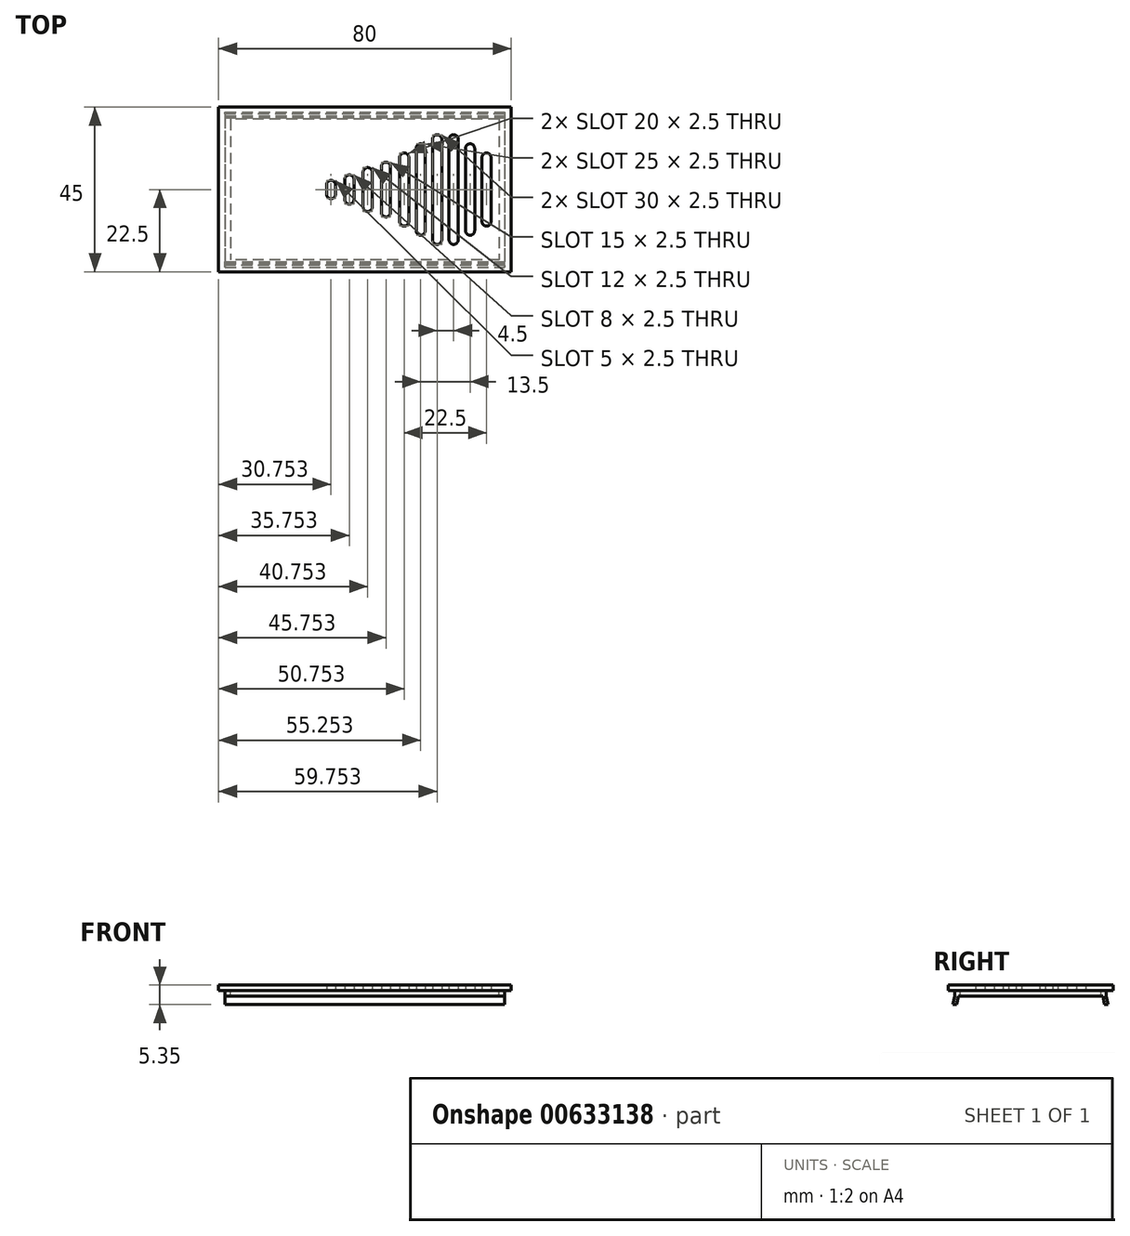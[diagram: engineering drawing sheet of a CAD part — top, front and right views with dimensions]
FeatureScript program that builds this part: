
annotation { "Feature Type Name" : "Feature", "Feature Type Description" : "" }
export const myFeature = defineFeature(function(context is Context, id is Id, definition is map)
    precondition{}
    {
        {
            var Q0;
            Q0=qCreatedBy(makeId("Top.planeOp"),FACE);
            var sketch = newSketch(context, id + "F0", { "sketchPlane" : qUnion([Q0])});
            skLineSegment(sketch, "E0.bottom", {"start": v(-39.19, 25) * mm, "end": v(40.81, 25) * mm});
            skLineSegment(sketch, "E0.top", {"start": v(-39.19, -20) * mm, "end": v(40.81, -20) * mm});
            skLineSegment(sketch, "E0.left", {"start": v(-39.19, 25) * mm, "end": v(-39.19, -20) * mm});
            skLineSegment(sketch, "E0.right", {"start": v(40.81, 25) * mm, "end": v(40.81, -20) * mm});
            skLineSegment(sketch, "E1.bottom", {"start": v(29.56, 15) * mm, "end": v(29.56, 15) * mm});
            skLineSegment(sketch, "E1.top", {"start": v(29.56, -10) * mm, "end": v(29.56, -10) * mm});
            skLineSegment(sketch, "E1.left", {"start": v(28.31, 13.75) * mm, "end": v(28.31, -8.75) * mm});
            skLineSegment(sketch, "E1.right", {"start": v(30.81, 13.75) * mm, "end": v(30.81, -8.75) * mm});
            skLineSegment(sketch, "E2.bottom", {"start": v(25.06, 17.5) * mm, "end": v(25.06, 17.5) * mm});
            skLineSegment(sketch, "E2.top", {"start": v(25.06, -12.5) * mm, "end": v(25.06, -12.5) * mm});
            skLineSegment(sketch, "E2.left", {"start": v(23.81, 16.25) * mm, "end": v(23.81, -11.25) * mm});
            skLineSegment(sketch, "E2.right", {"start": v(26.31, 16.25) * mm, "end": v(26.31, -11.25) * mm});
            skLineSegment(sketch, "E3.bottom", {"start": v(20.56, 17.5) * mm, "end": v(20.56, 17.5) * mm});
            skLineSegment(sketch, "E3.top", {"start": v(20.56, -12.5) * mm, "end": v(20.56, -12.5) * mm});
            skLineSegment(sketch, "E3.left", {"start": v(19.31, 16.25) * mm, "end": v(19.31, -11.25) * mm});
            skLineSegment(sketch, "E3.right", {"start": v(21.81, 16.25) * mm, "end": v(21.81, -11.25) * mm});
            skLineSegment(sketch, "E4.bottom", {"start": v(16.06, 15) * mm, "end": v(16.06, 15) * mm});
            skLineSegment(sketch, "E4.top", {"start": v(16.06, -10) * mm, "end": v(16.06, -10) * mm});
            skLineSegment(sketch, "E4.left", {"start": v(14.81, 13.75) * mm, "end": v(14.81, -8.75) * mm});
            skLineSegment(sketch, "E4.right", {"start": v(17.31, 13.75) * mm, "end": v(17.31, -8.75) * mm});
            skLineSegment(sketch, "E5.bottom", {"start": v(11.56, 12.5) * mm, "end": v(11.56, 12.5) * mm});
            skLineSegment(sketch, "E5.top", {"start": v(11.56, -7.5) * mm, "end": v(11.56, -7.5) * mm});
            skLineSegment(sketch, "E5.left", {"start": v(10.31, 11.25) * mm, "end": v(10.31, -6.25) * mm});
            skLineSegment(sketch, "E5.right", {"start": v(12.81, 11.25) * mm, "end": v(12.81, -6.25) * mm});
            skLineSegment(sketch, "E6.bottom", {"start": v(34.06, 12.5) * mm, "end": v(34.06, 12.5) * mm});
            skLineSegment(sketch, "E6.top", {"start": v(34.06, -7.5) * mm, "end": v(34.06, -7.5) * mm});
            skLineSegment(sketch, "E6.left", {"start": v(32.81, 11.25) * mm, "end": v(32.81, -6.25) * mm});
            skLineSegment(sketch, "E6.right", {"start": v(35.31, 11.25) * mm, "end": v(35.31, -6.25) * mm});
            skPoint(sketch, "E7.visualSharp", {"position": v(35.31, -7.5) * mm});
            skArc(sketch, "E7.filletArc", {"start": v(34.06, -7.5) * mm, "mid": v(34.95, -7.13) * mm, "end": v(35.31, -6.25) * mm});
            skPoint(sketch, "E8.visualSharp", {"position": v(32.81, -7.5) * mm});
            skArc(sketch, "E8.filletArc", {"start": v(32.81, -6.25) * mm, "mid": v(33.18, -7.13) * mm, "end": v(34.06, -7.5) * mm});
            skPoint(sketch, "E9.visualSharp", {"position": v(32.81, 12.5) * mm});
            skArc(sketch, "E9.filletArc", {"start": v(34.06, 12.5) * mm, "mid": v(33.18, 12.13) * mm, "end": v(32.81, 11.25) * mm});
            skPoint(sketch, "E10.visualSharp", {"position": v(35.31, 12.5) * mm});
            skArc(sketch, "E10.filletArc", {"start": v(35.31, 11.25) * mm, "mid": v(34.95, 12.13) * mm, "end": v(34.06, 12.5) * mm});
            skPoint(sketch, "E11.visualSharp", {"position": v(30.81, 15) * mm});
            skArc(sketch, "E11.filletArc", {"start": v(30.81, 13.75) * mm, "mid": v(30.45, 14.63) * mm, "end": v(29.56, 15) * mm});
            skPoint(sketch, "E12.visualSharp", {"position": v(28.31, 15) * mm});
            skArc(sketch, "E12.filletArc", {"start": v(29.56, 15) * mm, "mid": v(28.68, 14.63) * mm, "end": v(28.31, 13.75) * mm});
            skPoint(sketch, "E13.visualSharp", {"position": v(28.31, -10) * mm});
            skArc(sketch, "E13.filletArc", {"start": v(28.31, -8.75) * mm, "mid": v(28.68, -9.63) * mm, "end": v(29.56, -10) * mm});
            skPoint(sketch, "E14.visualSharp", {"position": v(30.81, -10) * mm});
            skArc(sketch, "E14.filletArc", {"start": v(29.56, -10) * mm, "mid": v(30.45, -9.63) * mm, "end": v(30.81, -8.75) * mm});
            skPoint(sketch, "E15.visualSharp", {"position": v(26.31, -12.5) * mm});
            skArc(sketch, "E15.filletArc", {"start": v(25.06, -12.5) * mm, "mid": v(25.95, -12.13) * mm, "end": v(26.31, -11.25) * mm});
            skPoint(sketch, "E16.visualSharp", {"position": v(23.81, -12.5) * mm});
            skArc(sketch, "E16.filletArc", {"start": v(23.81, -11.25) * mm, "mid": v(24.18, -12.13) * mm, "end": v(25.06, -12.5) * mm});
            skPoint(sketch, "E17.visualSharp", {"position": v(21.81, -12.5) * mm});
            skArc(sketch, "E17.filletArc", {"start": v(20.56, -12.5) * mm, "mid": v(21.45, -12.13) * mm, "end": v(21.81, -11.25) * mm});
            skPoint(sketch, "E18.visualSharp", {"position": v(19.31, -12.5) * mm});
            skArc(sketch, "E18.filletArc", {"start": v(19.31, -11.25) * mm, "mid": v(19.68, -12.13) * mm, "end": v(20.56, -12.5) * mm});
            skPoint(sketch, "E19.visualSharp", {"position": v(17.31, -10) * mm});
            skArc(sketch, "E19.filletArc", {"start": v(16.06, -10) * mm, "mid": v(16.95, -9.63) * mm, "end": v(17.31, -8.75) * mm});
            skPoint(sketch, "E20.visualSharp", {"position": v(14.81, -10) * mm});
            skArc(sketch, "E20.filletArc", {"start": v(14.81, -8.75) * mm, "mid": v(15.18, -9.63) * mm, "end": v(16.06, -10) * mm});
            skPoint(sketch, "E21.visualSharp", {"position": v(12.81, -7.5) * mm});
            skArc(sketch, "E21.filletArc", {"start": v(11.56, -7.5) * mm, "mid": v(12.45, -7.13) * mm, "end": v(12.81, -6.25) * mm});
            skPoint(sketch, "E22.visualSharp", {"position": v(10.31, -7.5) * mm});
            skArc(sketch, "E22.filletArc", {"start": v(10.31, -6.25) * mm, "mid": v(10.68, -7.13) * mm, "end": v(11.56, -7.5) * mm});
            skPoint(sketch, "E23.visualSharp", {"position": v(10.31, 12.5) * mm});
            skArc(sketch, "E23.filletArc", {"start": v(11.56, 12.5) * mm, "mid": v(10.68, 12.13) * mm, "end": v(10.31, 11.25) * mm});
            skPoint(sketch, "E24.visualSharp", {"position": v(12.81, 12.5) * mm});
            skArc(sketch, "E24.filletArc", {"start": v(12.81, 11.25) * mm, "mid": v(12.45, 12.13) * mm, "end": v(11.56, 12.5) * mm});
            skPoint(sketch, "E25.visualSharp", {"position": v(14.81, 15) * mm});
            skArc(sketch, "E25.filletArc", {"start": v(16.06, 15) * mm, "mid": v(15.18, 14.63) * mm, "end": v(14.81, 13.75) * mm});
            skPoint(sketch, "E26.visualSharp", {"position": v(17.31, 15) * mm});
            skArc(sketch, "E26.filletArc", {"start": v(17.31, 13.75) * mm, "mid": v(16.95, 14.63) * mm, "end": v(16.06, 15) * mm});
            skPoint(sketch, "E27.visualSharp", {"position": v(19.31, 17.5) * mm});
            skArc(sketch, "E27.filletArc", {"start": v(20.56, 17.5) * mm, "mid": v(19.68, 17.13) * mm, "end": v(19.31, 16.25) * mm});
            skPoint(sketch, "E28.visualSharp", {"position": v(21.81, 17.5) * mm});
            skArc(sketch, "E28.filletArc", {"start": v(21.81, 16.25) * mm, "mid": v(21.45, 17.13) * mm, "end": v(20.56, 17.5) * mm});
            skPoint(sketch, "E29.visualSharp", {"position": v(23.81, 17.5) * mm});
            skArc(sketch, "E29.filletArc", {"start": v(25.06, 17.5) * mm, "mid": v(24.18, 17.13) * mm, "end": v(23.81, 16.25) * mm});
            skPoint(sketch, "E30.visualSharp", {"position": v(26.31, 17.5) * mm});
            skArc(sketch, "E30.filletArc", {"start": v(26.31, 16.25) * mm, "mid": v(25.95, 17.13) * mm, "end": v(25.06, 17.5) * mm});
            skLineSegment(sketch, "E31", {"start": v(-39.19, 2.5) * mm, "end": v(40.81, 2.5) * mm, "construction": true});
            skLineSegment(sketch, "E32.bottom", {"start": v(6.56, -5) * mm, "end": v(6.56, -5) * mm});
            skLineSegment(sketch, "E32.top", {"start": v(6.56, 10) * mm, "end": v(6.56, 10) * mm});
            skLineSegment(sketch, "E32.left", {"start": v(5.31, -3.75) * mm, "end": v(5.31, 8.75) * mm});
            skLineSegment(sketch, "E32.right", {"start": v(7.81, -3.75) * mm, "end": v(7.81, 8.75) * mm});
            skLineSegment(sketch, "E33.bottom", {"start": v(1.56, -3.5) * mm, "end": v(1.56, -3.5) * mm});
            skLineSegment(sketch, "E33.top", {"start": v(1.56, 8.5) * mm, "end": v(1.56, 8.5) * mm});
            skLineSegment(sketch, "E33.left", {"start": v(0.31, -2.25) * mm, "end": v(0.31, 7.25) * mm});
            skLineSegment(sketch, "E33.right", {"start": v(2.81, -2.25) * mm, "end": v(2.81, 7.25) * mm});
            skPoint(sketch, "E34.visualSharp", {"position": v(5.31, -5) * mm});
            skArc(sketch, "E34.filletArc", {"start": v(5.31, -3.75) * mm, "mid": v(5.68, -4.63) * mm, "end": v(6.56, -5) * mm});
            skPoint(sketch, "E35.visualSharp", {"position": v(7.81, -5) * mm});
            skArc(sketch, "E35.filletArc", {"start": v(6.56, -5) * mm, "mid": v(7.45, -4.63) * mm, "end": v(7.81, -3.75) * mm});
            skPoint(sketch, "E36.visualSharp", {"position": v(5.31, 10) * mm});
            skArc(sketch, "E36.filletArc", {"start": v(6.56, 10) * mm, "mid": v(5.68, 9.63) * mm, "end": v(5.31, 8.75) * mm});
            skPoint(sketch, "E37.visualSharp", {"position": v(7.81, 10) * mm});
            skArc(sketch, "E37.filletArc", {"start": v(7.81, 8.75) * mm, "mid": v(7.45, 9.63) * mm, "end": v(6.56, 10) * mm});
            skPoint(sketch, "E38.visualSharp", {"position": v(2.81, -3.5) * mm});
            skArc(sketch, "E38.filletArc", {"start": v(1.56, -3.5) * mm, "mid": v(2.45, -3.13) * mm, "end": v(2.81, -2.25) * mm});
            skPoint(sketch, "E39.visualSharp", {"position": v(0.31, -3.5) * mm});
            skArc(sketch, "E39.filletArc", {"start": v(0.31, -2.25) * mm, "mid": v(0.68, -3.13) * mm, "end": v(1.56, -3.5) * mm});
            skPoint(sketch, "E40.visualSharp", {"position": v(0.31, 8.5) * mm});
            skArc(sketch, "E40.filletArc", {"start": v(1.56, 8.5) * mm, "mid": v(0.68, 8.13) * mm, "end": v(0.31, 7.25) * mm});
            skPoint(sketch, "E41.visualSharp", {"position": v(2.81, 8.5) * mm});
            skArc(sketch, "E41.filletArc", {"start": v(2.81, 7.25) * mm, "mid": v(2.45, 8.13) * mm, "end": v(1.56, 8.5) * mm});
            skLineSegment(sketch, "E42.bottom", {"start": v(-3.44, -1.5) * mm, "end": v(-3.44, -1.5) * mm});
            skLineSegment(sketch, "E42.top", {"start": v(-3.44, 6.5) * mm, "end": v(-3.44, 6.5) * mm});
            skLineSegment(sketch, "E42.left", {"start": v(-4.69, -0.25) * mm, "end": v(-4.69, 5.25) * mm});
            skLineSegment(sketch, "E42.right", {"start": v(-2.19, -0.25) * mm, "end": v(-2.19, 5.25) * mm});
            skPoint(sketch, "E43.visualSharp", {"position": v(-4.69, -1.5) * mm});
            skArc(sketch, "E43.filletArc", {"start": v(-4.69, -0.25) * mm, "mid": v(-4.32, -1.13) * mm, "end": v(-3.44, -1.5) * mm});
            skPoint(sketch, "E44.visualSharp", {"position": v(-2.19, -1.5) * mm});
            skArc(sketch, "E44.filletArc", {"start": v(-3.44, -1.5) * mm, "mid": v(-2.55, -1.13) * mm, "end": v(-2.19, -0.25) * mm});
            skPoint(sketch, "E45.visualSharp", {"position": v(-2.19, 6.5) * mm});
            skArc(sketch, "E45.filletArc", {"start": v(-2.19, 5.25) * mm, "mid": v(-2.55, 6.13) * mm, "end": v(-3.44, 6.5) * mm});
            skPoint(sketch, "E46.visualSharp", {"position": v(-4.69, 6.5) * mm});
            skArc(sketch, "E46.filletArc", {"start": v(-3.44, 6.5) * mm, "mid": v(-4.32, 6.13) * mm, "end": v(-4.69, 5.25) * mm});
            skLineSegment(sketch, "E47.bottom", {"start": v(-8.44, 0) * mm, "end": v(-8.44, 0) * mm});
            skLineSegment(sketch, "E47.top", {"start": v(-8.44, 5) * mm, "end": v(-8.44, 5) * mm});
            skLineSegment(sketch, "E47.left", {"start": v(-9.69, 1.25) * mm, "end": v(-9.69, 3.75) * mm});
            skLineSegment(sketch, "E47.right", {"start": v(-7.19, 1.25) * mm, "end": v(-7.19, 3.75) * mm});
            skPoint(sketch, "E48.visualSharp", {"position": v(-7.19, 0) * mm});
            skArc(sketch, "E48.filletArc", {"start": v(-8.44, 0) * mm, "mid": v(-7.55, 0.37) * mm, "end": v(-7.19, 1.25) * mm});
            skPoint(sketch, "E49.visualSharp", {"position": v(-9.69, 0) * mm});
            skArc(sketch, "E49.filletArc", {"start": v(-9.69, 1.25) * mm, "mid": v(-9.32, 0.37) * mm, "end": v(-8.44, 0) * mm});
            skPoint(sketch, "E50.visualSharp", {"position": v(-9.69, 5) * mm});
            skArc(sketch, "E50.filletArc", {"start": v(-8.44, 5) * mm, "mid": v(-9.32, 4.63) * mm, "end": v(-9.69, 3.75) * mm});
            skPoint(sketch, "E51.visualSharp", {"position": v(-7.19, 5) * mm});
            skArc(sketch, "E51.filletArc", {"start": v(-7.19, 3.75) * mm, "mid": v(-7.55, 4.63) * mm, "end": v(-8.44, 5) * mm});
            skSolve(sketch);
        }
        {
            var Q0;
            Q0=makeQuery(id+"F0.imprint","IMPRINT",FACE,{"disambiguationData":[TD([[makeQuery(id+"F0.imprint","IMPRINT",EDGE,{"derivedFrom":sQuery(id+"F0.wireOp",EDGE,"E0.bottom")}),-1.0]])]});
            extrude(context, id + "F1", {"entities" : qUnion([Q0]), "depth" : 1.5 * mm, "offsetDistance" : 25 * mm});
        }
        {
            var Q0;
            Q0=makeQuery(id+"F1.opExtrude","CAP_FACE",FACE,{"disambiguationData":[OSD([sQuery(id+"F0.wireOp",EDGE,"E0.bottom"),sQuery(id+"F0.wireOp",EDGE,"E0.top"),sQuery(id+"F0.wireOp",EDGE,"E0.left"),sQuery(id+"F0.wireOp",EDGE,"E0.right"),sQuery(id+"F0.wireOp",EDGE,"E1.bottom"),sQuery(id+"F0.wireOp",EDGE,"E1.top"),sQuery(id+"F0.wireOp",EDGE,"E1.left"),sQuery(id+"F0.wireOp",EDGE,"E1.right"),sQuery(id+"F0.wireOp",EDGE,"E2.bottom"),sQuery(id+"F0.wireOp",EDGE,"E2.top"),sQuery(id+"F0.wireOp",EDGE,"E2.left"),sQuery(id+"F0.wireOp",EDGE,"E2.right"),sQuery(id+"F0.wireOp",EDGE,"E3.bottom"),sQuery(id+"F0.wireOp",EDGE,"E3.top"),sQuery(id+"F0.wireOp",EDGE,"E3.left"),sQuery(id+"F0.wireOp",EDGE,"E3.right"),sQuery(id+"F0.wireOp",EDGE,"E4.bottom"),sQuery(id+"F0.wireOp",EDGE,"E4.top"),sQuery(id+"F0.wireOp",EDGE,"E4.left"),sQuery(id+"F0.wireOp",EDGE,"E4.right"),sQuery(id+"F0.wireOp",EDGE,"E5.bottom"),sQuery(id+"F0.wireOp",EDGE,"E5.top"),sQuery(id+"F0.wireOp",EDGE,"E5.left"),sQuery(id+"F0.wireOp",EDGE,"E5.right"),sQuery(id+"F0.wireOp",EDGE,"E6.bottom"),sQuery(id+"F0.wireOp",EDGE,"E6.top"),sQuery(id+"F0.wireOp",EDGE,"E6.left"),sQuery(id+"F0.wireOp",EDGE,"E6.right")])],"isStart":true});
            var sketch = newSketch(context, id + "F2", { "sketchPlane" : qUnion([Q0])});
            skLineSegment(sketch, "E52", {"start": v(40.81, 20) * mm, "end": v(40.81, -25) * mm, "construction": true});
            skLineSegment(sketch, "E53.bottom", {"start": v(39.01, -23.2) * mm, "end": v(-37.39, -23.2) * mm});
            skLineSegment(sketch, "E53.top", {"start": v(39.01, 18.2) * mm, "end": v(-37.39, 18.2) * mm});
            skLineSegment(sketch, "E53.left", {"start": v(39.01, -23.2) * mm, "end": v(39.01, 18.2) * mm});
            skLineSegment(sketch, "E53.right", {"start": v(-37.39, -23.2) * mm, "end": v(-37.39, 18.2) * mm});
            skLineSegment(sketch, "E54.bottom", {"start": v(37.51, -21.7) * mm, "end": v(-35.89, -21.7) * mm});
            skLineSegment(sketch, "E54.top", {"start": v(37.51, 16.7) * mm, "end": v(-35.89, 16.7) * mm});
            skLineSegment(sketch, "E54.left", {"start": v(37.51, -21.7) * mm, "end": v(37.51, 16.7) * mm});
            skLineSegment(sketch, "E54.right", {"start": v(-35.89, -21.7) * mm, "end": v(-35.89, 16.7) * mm});
            skSolve(sketch);
        }
        {
            var Q0;
            Q0 = qSketchRegion(id + "F2", true);
            extrude(context, id + "F3", {"entities" : qUnion([Q0]), "operationType" : NewBodyOperationType.ADD, "depth" : 1.5 * mm, "offsetDistance" : 25 * mm});
        }
        {
            var Q0;
            Q0=makeQuery(id+"F3.opExtrude","SWEPT_FACE",FACE,{"disambiguationData":[OSD([sQuery(id+"F2.wireOp",EDGE,"E53.left")])]});
            var sketch = newSketch(context, id + "F4", { "sketchPlane" : qUnion([Q0])});
            skLineSegment(sketch, "E55", {"start": v(23.2, -1.5) * mm, "end": v(23.7, -3.85) * mm});
            skLineSegment(sketch, "E56", {"start": v(23.7, -3.85) * mm, "end": v(22.7, -3.85) * mm});
            skLineSegment(sketch, "E57", {"start": v(22.7, -3.85) * mm, "end": v(22.2, -1.5) * mm});
            skLineSegment(sketch, "E58", {"start": v(22.2, -1.5) * mm, "end": v(23.2, -1.5) * mm});
            skLineSegment(sketch, "E59", {"start": v(2.5, -1.5) * mm, "end": v(2.5, -4.91) * mm, "construction": true});
            skLineSegment(sketch, "E60.MirrorCS", {"start": v(-17.7, -3.85) * mm, "end": v(-17.2, -1.5) * mm});
            skLineSegment(sketch, "E61.MirrorCS", {"start": v(-18.7, -3.85) * mm, "end": v(-17.7, -3.85) * mm});
            skLineSegment(sketch, "E62.MirrorCS", {"start": v(-18.2, -1.5) * mm, "end": v(-18.7, -3.85) * mm});
            skLineSegment(sketch, "E63.MirrorCS", {"start": v(-17.2, -1.5) * mm, "end": v(-18.2, -1.5) * mm});
            skSolve(sketch);
        }
        {
            var Q0;
            Q0=makeQuery(id+"F4.imprint","IMPRINT",FACE,{"disambiguationData":[TD([[makeQuery(id+"F4.imprint","IMPRINT",EDGE,{"derivedFrom":sQuery(id+"F4.wireOp",EDGE,"E55")}),-1.0]])]});
            extrude(context, id + "F5", {"entities" : qUnion([Q0]), "operationType" : NewBodyOperationType.ADD, "oppositeDirection" : true, "depth" : 76.4 * mm, "offsetDistance" : 25 * mm});
        }
        {
            var Q0;
            Q0 = qSketchRegion(id + "F4", true);
            extrude(context, id + "F6", {"entities" : qUnion([Q0]), "operationType" : NewBodyOperationType.ADD, "oppositeDirection" : true, "depth" : 76.4 * mm, "offsetDistance" : 25 * mm});
        }
    });
